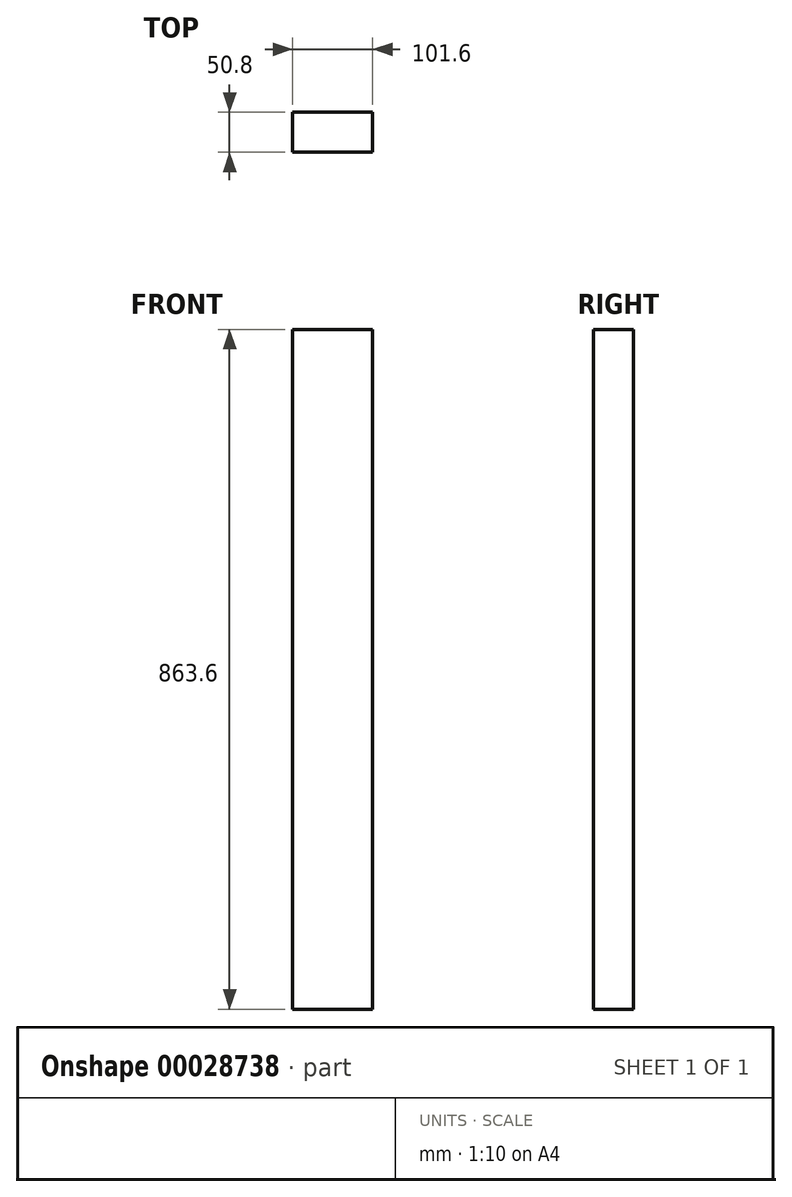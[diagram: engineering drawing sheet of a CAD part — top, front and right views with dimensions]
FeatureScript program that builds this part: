
annotation { "Feature Type Name" : "Feature", "Feature Type Description" : "" }
export const myFeature = defineFeature(function(context is Context, id is Id, definition is map)
    precondition{}
    {
        {
            var Q0;
            Q0=qCreatedBy(makeId("Top.planeOp"),FACE);
            var sketch = newSketch(context, id + "F0", { "sketchPlane" : qUnion([Q0])});
            skLineSegment(sketch, "E0.bottom", {"start": v(-29.43, 28.2) * mm, "end": v(72.17, 28.2) * mm});
            skLineSegment(sketch, "E0.top", {"start": v(-29.43, -22.6) * mm, "end": v(72.17, -22.6) * mm});
            skLineSegment(sketch, "E0.left", {"start": v(-29.43, 28.2) * mm, "end": v(-29.43, -22.6) * mm});
            skLineSegment(sketch, "E0.right", {"start": v(72.17, 28.2) * mm, "end": v(72.17, -22.6) * mm});
            skSolve(sketch);
        }
        {
            var Q0;
            Q0=makeQuery(id+"F0.imprint","IMPRINT",FACE,{"disambiguationData":[TD([[makeQuery(id+"F0.imprint","IMPRINT",EDGE,{"derivedFrom":sQuery(id+"F0.wireOp",EDGE,"E0.bottom")}),-1.0]])]});
            extrude(context, id + "F1", {"entities" : qUnion([Q0]), "depth" : 863.6 * mm});
        }
    });
